# Revit family: Wicstyle77FP_Single_open_OUT_door_EI30_T30
name_source: partatom
category: Doors
revit_build: Autodesk Revit Architecture 2014 (Build: 20130308_1515(x64)
units: mm (PartAtom-declared; Revit-internal decimal feet)

## types (1)
- Wicstyle77FP_Single_open_OUT_door_EI30_T30
    Bottom 1020459 = Yes
    Bottom 1020463 = No
    Bottom 1021353 = No
    Bottom Offset = 26 mm
    Clearance passage dimensions = Single-leaf 1,362 x 2,500 mm, Double-leaf 2,500 x 2,500 mm, Fixed glazing element height up to 3,500 mm, unlimited width
    Date of publishing = 3/14/2015
    Description = WICSTYLE 77FP provides 30 minutes’ fire resistance with profile elevations that are identical to a WICSTYLE 77 standard door, meaning that it ensures all the doors in your building have the same design. Consequently, this range fulfils the requirements of class EI30 and/or class T30/F30 for single and double-leaf doors with large leaf dimensions, without the need for fire protection inserts in this class.
    Design country = Germany
    Door Offset = 40 mm
    Edition number = 1
    Filling thickness = 23 or 36 mm Type 30 pyrostop glass
    Filling weights = Up to 200 kg
    Fire protection class in accordance with DIN 4102 = T30-1 and T30-2, F30 glazing
    Fire protection class in accordance with DIN EN 13501-2 = EI30-1, EI30 glazing
    Frame 1020449 = Yes
    Frame 1020455 = No
    Frame 1021351 = No
    Frame 1021361 = No
    Frame Depth = 77 mm  [stored 0.252625 ft]
    Frame Material = WICONA - Aluminium - RAL7016 - Anthracite Grey - Matt
    Frame Width = 67 mm
    Frame Width 2 = 52 mm
    Frame Width 3 = 43 mm
    Function = Interior
    Glass Material = WICONA -  Glass
    Handle Material = Aluminium
    Height = 2100 mm
    Leaf Height = 2022 mm  [stored 6.63386 ft]
    Leaf Material = WICONA - Aluminium - RAL7016 - Anthracite Grey - Matt
    Leaf Width = 896 mm  [stored 2.93963 ft]
    Manufacturer = Wicona
    Manufacturer country = Germany
    Manufacturer name = Wicona
    Material main = Aluminium
    Material secondary = Glass
    Model = Wicstyle 77FP
    Nominal height = 210000
    Nominal width = 140000
    Opening Line Lenght = 896 mm  [stored 2.93963 ft]
    Product Guid = 0a2d15cc-3e25-4d95-9584-ec63cf4c32b4
    Product SKU = WICSTYLE_77_FP_D
    Product data url = http://bimobject.com
    Product family = Windows & Doors
    Product group = Windows
    QR code = http://bimobject.com
    Sash 1020445 = Yes
    Sash 1021358 = No
    Sash 1021359 = No
    Threshold 1021235 = Yes
    Threshold 1021236 = No
    URL = http://www.wicona.com
    Wall Closure = By host
    Weight Net (Kg) = 0
    Width = 1000 mm  [stored 3.28084 ft]

note: [stored X ft] marks values corroborated as IEEE doubles in the binary element streams (Revit-internal decimal feet)

## geometry (parser evidence)
native form markers: Blend x2, Sweep x11
no freeform markers — native parametric forms only
